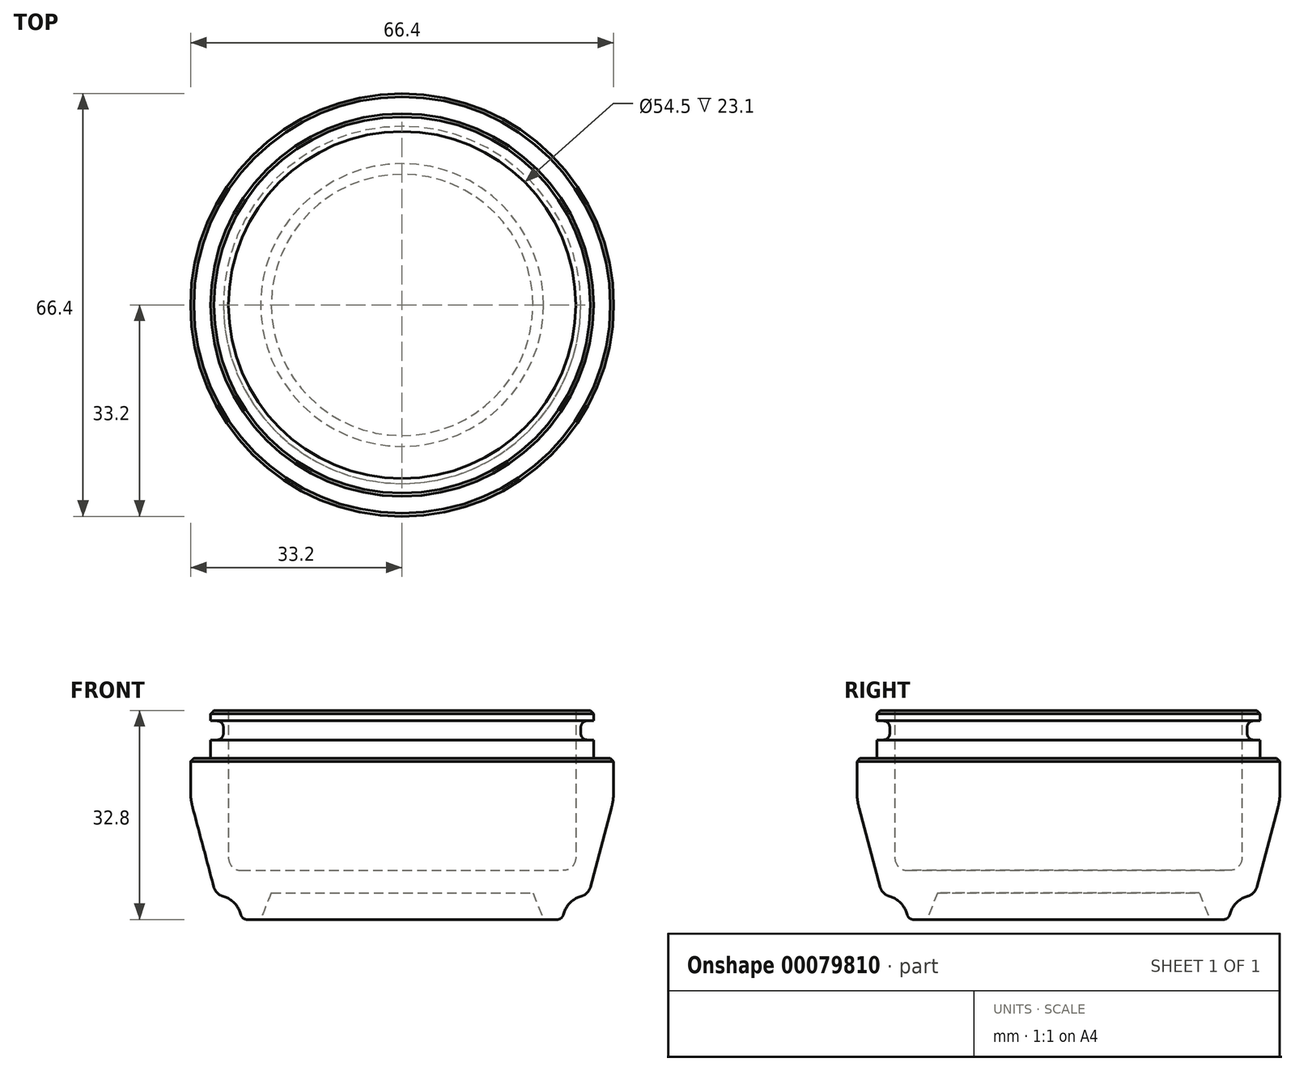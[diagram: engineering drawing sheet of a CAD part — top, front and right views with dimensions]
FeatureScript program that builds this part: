
annotation { "Feature Type Name" : "Feature", "Feature Type Description" : "" }
export const myFeature = defineFeature(function(context is Context, id is Id, definition is map)
    precondition{}
    {
        {
            var Q0;
            Q0=qCreatedBy(makeId("Front.planeOp"),FACE);
            var sketch = newSketch(context, id + "F0", { "sketchPlane" : qUnion([Q0])});
            skLineSegment(sketch, "E0", {"start": v(-27.25, -6.67) * mm, "end": v(-27.25, 18.43) * mm});
            skLineSegment(sketch, "E1", {"start": v(-27.25, 18.43) * mm, "end": v(-30.05, 18.43) * mm});
            skLineSegment(sketch, "E2", {"start": v(-30.05, 18.43) * mm, "end": v(-30.05, 16.83) * mm});
            skLineSegment(sketch, "E3", {"start": v(-30.05, 16.83) * mm, "end": v(-28.05, 16.83) * mm});
            skLineSegment(sketch, "E4", {"start": v(-28.05, 16.83) * mm, "end": v(-28.05, 13.83) * mm});
            skLineSegment(sketch, "E5", {"start": v(-28.05, 13.83) * mm, "end": v(-30.05, 13.83) * mm});
            skLineSegment(sketch, "E6", {"start": v(-30.05, 13.83) * mm, "end": v(-30.05, 10.93) * mm});
            skLineSegment(sketch, "E7", {"start": v(-30.05, 10.93) * mm, "end": v(-33.2, 10.93) * mm});
            skLineSegment(sketch, "E8", {"start": v(-33.2, 10.93) * mm, "end": v(-33.2, 4.43) * mm});
            skLineSegment(sketch, "E9", {"start": v(-33.2, 4.43) * mm, "end": v(-29.2, -10.57) * mm});
            skLineSegment(sketch, "E10", {"start": v(-29.2, -10.57) * mm, "end": v(-25.2, -10.57) * mm});
            skLineSegment(sketch, "E11", {"start": v(-25.2, -10.57) * mm, "end": v(-25.2, -14.37) * mm});
            skLineSegment(sketch, "E12", {"start": v(-25.2, -14.37) * mm, "end": v(-22.2, -14.37) * mm});
            skLineSegment(sketch, "E13", {"start": v(-20.53, -10.17) * mm, "end": v(-22.2, -14.37) * mm});
            skLineSegment(sketch, "E14", {"start": v(-20.53, -10.17) * mm, "end": v(0, -10.17) * mm});
            skLineSegment(sketch, "E15", {"start": v(0, -10.17) * mm, "end": v(0, -6.67) * mm});
            skLineSegment(sketch, "E16", {"start": v(0, -6.67) * mm, "end": v(-27.25, -6.67) * mm});
            skSolve(sketch);
        }
        {
            var Q0;
            Q0=makeQuery(id+"F0.imprint","IMPRINT",FACE,{"disambiguationData":[TD([[makeQuery(id+"F0.imprint","IMPRINT",EDGE,{"derivedFrom":sQuery(id+"F0.wireOp",EDGE,"E0")}),1.0]])]});
            var Q1;
            Q1=sQuery(id+"F0.wireOp",EDGE,"E15");
            revolve(context, id + "F1", {"entities" : qUnion([Q0]), "axis" : qUnion([Q1]), "revolveType" : RevolveType.FULL});
        }
        {
            var Q0;
            Q0=makeQuery(id+"F1.opRevolve","SWEPT_EDGE",EDGE,{"disambiguationData":[OSD([sQuery(id+"F0.wireOp",EDGE,"E10"),sQuery(id+"F0.wireOp",EDGE,"E11")])]});
            fillet(context, id + "F2", {"entities" : qUnion([Q0]), "radius" : 4 * mm, "tangentPropagation" : true, "allowEdgeOverflow" : false});
        }
        {
            var Q0;
            Q0=makeQuery(id+"F1.opRevolve","SWEPT_EDGE",EDGE,{"disambiguationData":[OSD([sQuery(id+"F0.wireOp",EDGE,"E0"),sQuery(id+"F0.wireOp",EDGE,"E16")])]});
            fillet(context, id + "F3", {"entities" : qUnion([Q0]), "radius" : 2 * mm, "tangentPropagation" : true, "allowEdgeOverflow" : false});
        }
        {
            var Q0;
            Q0=makeQuery(id+"F2.opFillet","BLEND_EDGE",EDGE,{"blendedFrom":[makeQuery(id+"F1.opRevolve","SWEPT_EDGE",EDGE,{"disambiguationData":[OSD([sQuery(id+"F0.wireOp",EDGE,"E10"),sQuery(id+"F0.wireOp",EDGE,"E11")])]}),makeQuery(id+"F1.opRevolve","SWEPT_FACE",FACE,{"disambiguationData":[OSD([sQuery(id+"F0.wireOp",EDGE,"E12")])]})],"blendedInto":[makeQuery(id+"F1.opRevolve","SWEPT_FACE",FACE,{"disambiguationData":[OSD([sQuery(id+"F0.wireOp",EDGE,"E12")])]})]});
            fillet(context, id + "F4", {"entities" : qUnion([Q0]), "radius" : 1 * mm, "tangentPropagation" : true, "allowEdgeOverflow" : false});
        }
        {
            var Q0;
            Q0=makeQuery(id+"F1.opRevolve","SWEPT_EDGE",EDGE,{"disambiguationData":[OSD([sQuery(id+"F0.wireOp",EDGE,"E9"),sQuery(id+"F0.wireOp",EDGE,"E10")])]});
            fillet(context, id + "F5", {"entities" : qUnion([Q0]), "radius" : 2 * mm, "tangentPropagation" : true, "allowEdgeOverflow" : false});
        }
        {
            var Q0;
            Q0=makeQuery(id+"F1.opRevolve","SWEPT_EDGE",EDGE,{"disambiguationData":[OSD([sQuery(id+"F0.wireOp",EDGE,"E8"),sQuery(id+"F0.wireOp",EDGE,"E9")])]});
            fillet(context, id + "F8", {"entities" : qUnion([Q0]), "radius" : 10 * mm, "tangentPropagation" : true, "allowEdgeOverflow" : false});
        }
        {
            var Q0;
            Q0=makeQuery(id+"F1.opRevolve","SWEPT_EDGE",EDGE,{"disambiguationData":[OSD([sQuery(id+"F0.wireOp",EDGE,"E1"),sQuery(id+"F0.wireOp",EDGE,"E2")])]});
            chamfer(context, id + "F6", {"entities" : qUnion([Q0]), "width" : 0.5 * mm, "tangentPropagation" : true});
        }
        {
            var Q0;
            Q0=makeQuery(id+"F1.opRevolve","SWEPT_EDGE",EDGE,{"disambiguationData":[OSD([sQuery(id+"F0.wireOp",EDGE,"E7"),sQuery(id+"F0.wireOp",EDGE,"E8")])]});
            chamfer(context, id + "F9", {"entities" : qUnion([Q0]), "width" : 0.5 * mm, "tangentPropagation" : true});
        }
        {
            var Q0;
            Q0=makeQuery(id+"F1.opRevolve","SWEPT_EDGE",EDGE,{"disambiguationData":[OSD([sQuery(id+"F0.wireOp",EDGE,"E3"),sQuery(id+"F0.wireOp",EDGE,"E4")])]});
            var Q1;
            Q1=makeQuery(id+"F1.opRevolve","SWEPT_EDGE",EDGE,{"disambiguationData":[OSD([sQuery(id+"F0.wireOp",EDGE,"E4"),sQuery(id+"F0.wireOp",EDGE,"E5")])]});
            fillet(context, id + "F7", {"entities" : qUnion([Q0, Q1]), "radius" : 1 * mm, "tangentPropagation" : true, "allowEdgeOverflow" : false});
        }
    });
